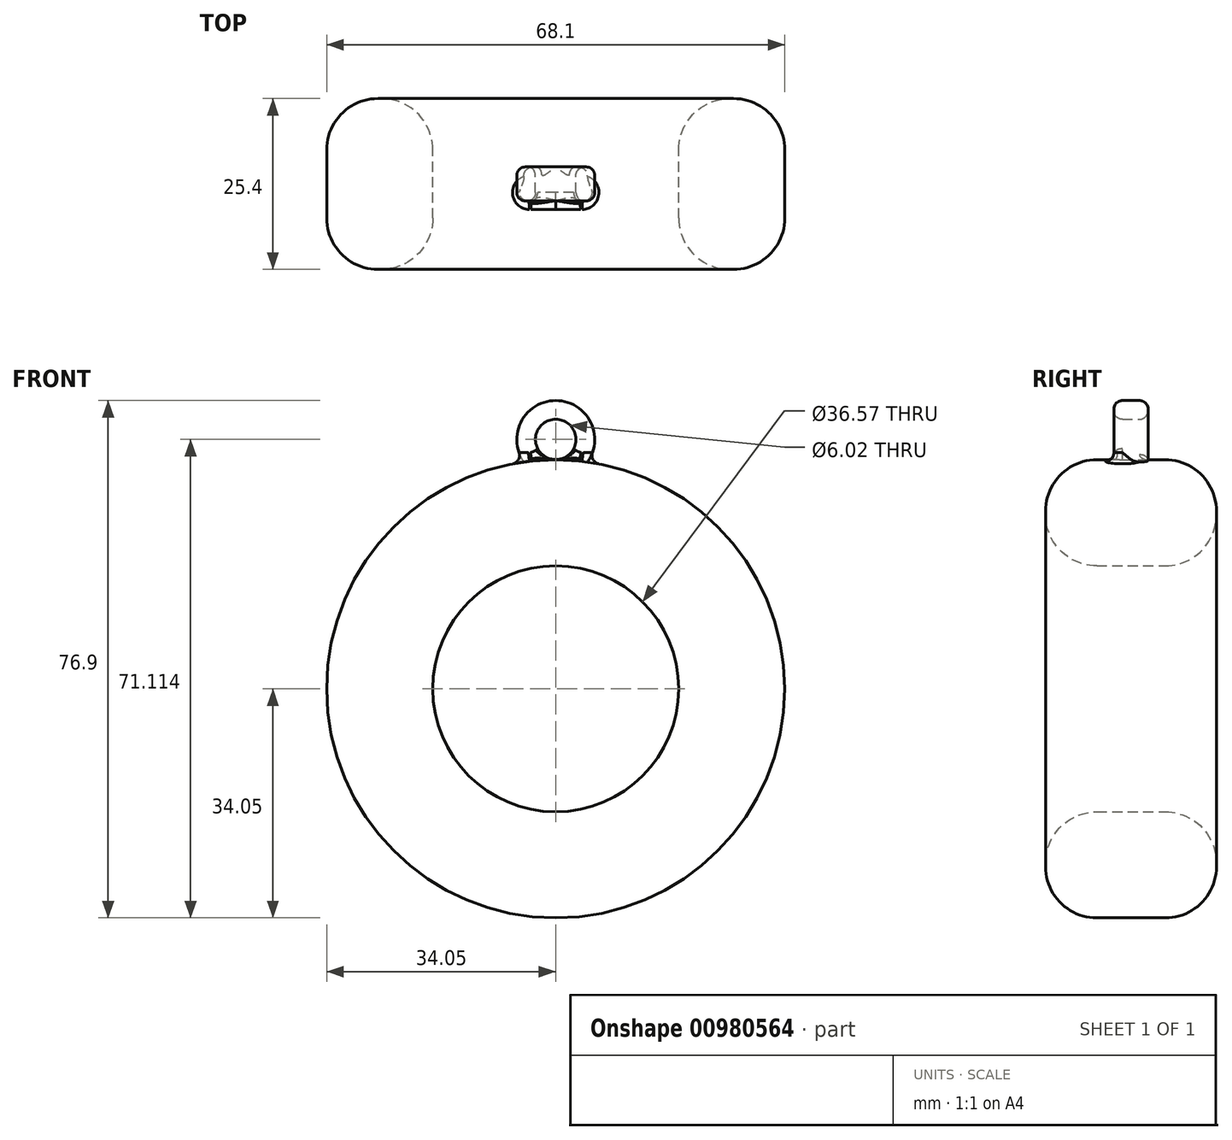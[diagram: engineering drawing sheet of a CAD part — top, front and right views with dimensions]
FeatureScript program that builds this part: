
annotation { "Feature Type Name" : "Feature", "Feature Type Description" : "" }
export const myFeature = defineFeature(function(context is Context, id is Id, definition is map)
    precondition{}
    {
        {
            var Q0;
            Q0=qCreatedBy(makeId("Front.planeOp"),FACE);
            var sketch = newSketch(context, id + "F0", { "sketchPlane" : qUnion([Q0])});
            skCircle(sketch, "E0", {"center": v(0, 0) * mm, "radius": 34.05 * mm});
            skCircle(sketch, "E1", {"center": v(0, 0) * mm, "radius": 18.29 * mm});
            skCircle(sketch, "E2", {"center": v(0, 37.06) * mm, "radius": 5.79 * mm});
            skCircle(sketch, "E3", {"center": v(0, 37.06) * mm, "radius": 3.01 * mm});
            skSolve(sketch);
        }
        {
            var Q0;
            Q0=makeQuery(id+"F0.imprint","IMPRINT",FACE,{"disambiguationData":[TD([[makeQuery(id+"F0.imprint","IMPRINT",EDGE,{"derivedFrom":sQuery(id+"F0.wireOp",EDGE,"E0")}),1.0]])]});
            var Q1;
            Q1=makeQuery(id+"F0.imprint","IMPRINT",FACE,{"disambiguationData":[TD([[makeQuery(id+"F0.imprint","IMPRINT",EDGE,{"derivedFrom":sQuery(id+"F0.wireOp",EDGE,"E1")}),-1.0]])]});
            extrude(context, id + "F1", {"entities" : qUnion([Q0, Q1]), "endBound" : BoundingType.SYMMETRIC, "depth" : 25.4 * mm, "offsetDistance" : 25.4 * mm});
        }
        {
            var Q0;
            Q0=makeQuery(id+"F1.opExtrude","CAP_FACE",FACE,{"disambiguationData":[OSD([sQuery(id+"F0.wireOp",EDGE,"E0"),sQuery(id+"F0.wireOp",EDGE,"E1")])],"isStart":false});
            var Q1;
            Q1=makeQuery(id+"F1.opExtrude","CAP_FACE",FACE,{"disambiguationData":[OSD([sQuery(id+"F0.wireOp",EDGE,"E0"),sQuery(id+"F0.wireOp",EDGE,"E1")])],"isStart":true});
            fillet(context, id + "F2", {"entities" : qUnion([Q0, Q1]), "radius" : 7.62 * mm, "tangentPropagation" : true, "allowEdgeOverflow" : false});
        }
        {
            var Q0;
            Q0 = qSketchRegion(id + "F0", true);
            extrude(context, id + "F3", {"entities" : qUnion([Q0]), "operationType" : NewBodyOperationType.ADD, "endBound" : BoundingType.SYMMETRIC, "depth" : 5.08 * mm, "offsetDistance" : 25.4 * mm});
        }
        {
            var Q0;
            Q0=makeQuery(id+"F3.opExtrude","CAP_EDGE",EDGE,{"disambiguationData":[OSD([sQuery(id+"F0.wireOp",EDGE,"E2")])],"isStart":true});
            var Q1;
            Q1=makeQuery(id+"F3.opExtrude","CAP_EDGE",EDGE,{"disambiguationData":[OSD([sQuery(id+"F0.wireOp",EDGE,"E3")])],"isStart":true});
            var Q2;
            Q2=makeQuery(id+"F3.opExtrude","CAP_FACE",FACE,{"disambiguationData":[OSD([sQuery(id+"F0.wireOp",EDGE,"E0"),sQuery(id+"F0.wireOp",EDGE,"E1"),sQuery(id+"F0.wireOp",EDGE,"E2"),sQuery(id+"F0.wireOp",EDGE,"E3")])],"isStart":false});
            fillet(context, id + "F4", {"entities" : qUnion([Q0, Q1, Q2]), "radius" : 1.27 * mm, "tangentPropagation" : true, "allowEdgeOverflow" : false});
        }
    });
